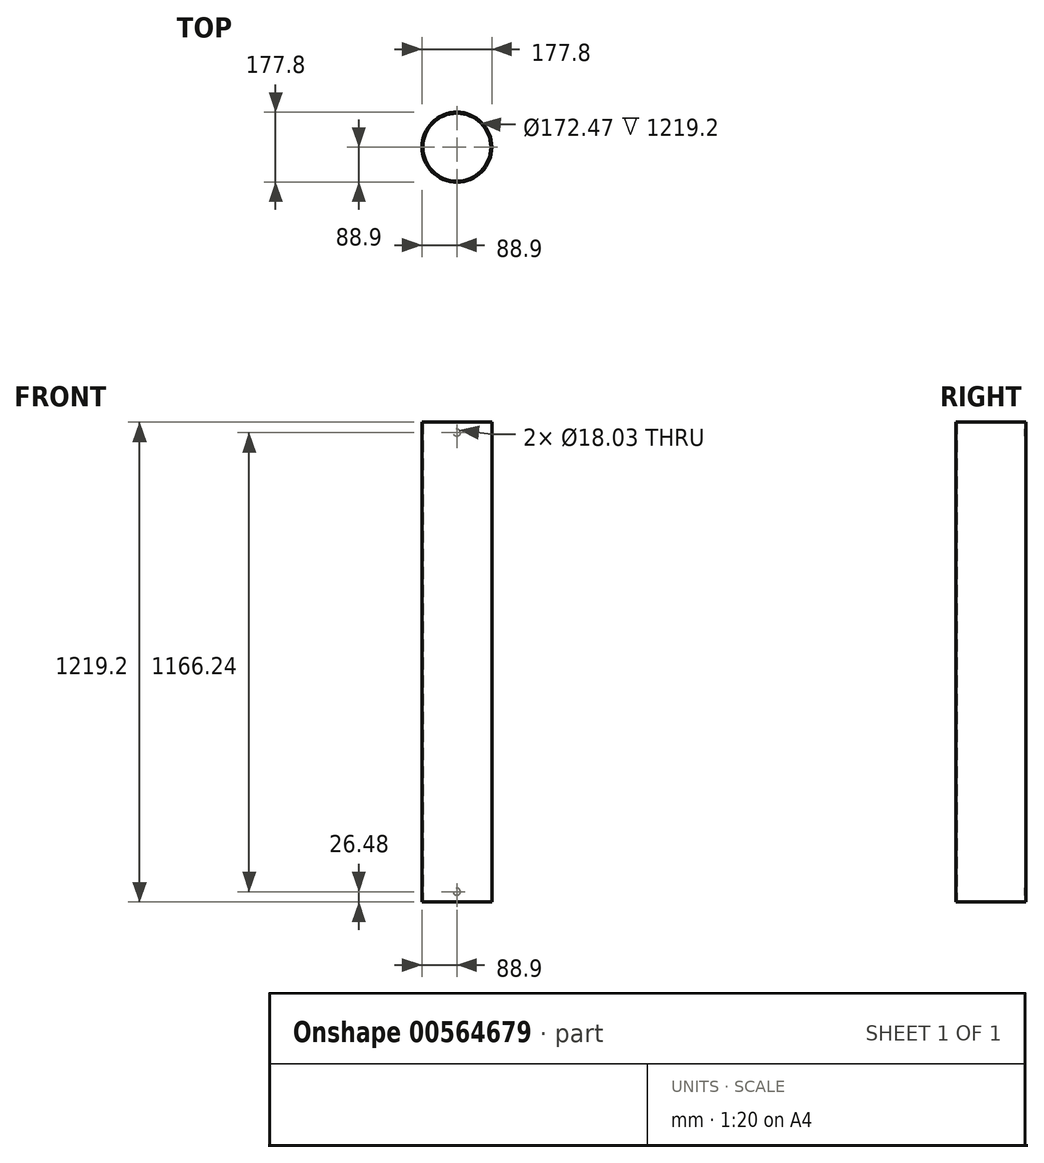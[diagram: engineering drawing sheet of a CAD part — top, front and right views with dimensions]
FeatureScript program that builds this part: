
annotation { "Feature Type Name" : "Feature", "Feature Type Description" : "" }
export const myFeature = defineFeature(function(context is Context, id is Id, definition is map)
    precondition{}
    {
        {
            var Q0;
            Q0=qCreatedBy(makeId("Top.planeOp"),FACE);
            var sketch = newSketch(context, id + "F0", { "sketchPlane" : qUnion([Q0])});
            skCircle(sketch, "E0", {"center": v(0, 0) * mm, "radius": 88.9 * mm});
            skCircle(sketch, "E1", {"center": v(0, 0) * mm, "radius": 86.23 * mm});
            skSolve(sketch);
        }
        {
            var Q0;
            Q0 = qSketchRegion(id + "F0", true);
            extrude(context, id + "F1", {"entities" : qUnion([Q0]), "depth" : 1219.2 * mm, "offsetDistance" : 25.4 * mm});
        }
        {
            var Q0;
            Q0=qCreatedBy(makeId("Front.planeOp"),FACE);
            var sketch = newSketch(context, id + "F2", { "sketchPlane" : qUnion([Q0])});
            skCircle(sketch, "E2", {"center": v(0, 1192.72) * mm, "radius": 9.02 * mm});
            skCircle(sketch, "E3", {"center": v(0, 26.48) * mm, "radius": 9.02 * mm});
            skSolve(sketch);
        }
        {
            var Q0;
            Q0 = qSketchRegion(id + "F2", true);
            extrude(context, id + "F3", {"entities" : qUnion([Q0]), "operationType" : NewBodyOperationType.REMOVE, "oppositeDirection" : true, "depth" : 203.2 * mm, "offsetDistance" : 25.4 * mm});
        }
    });
